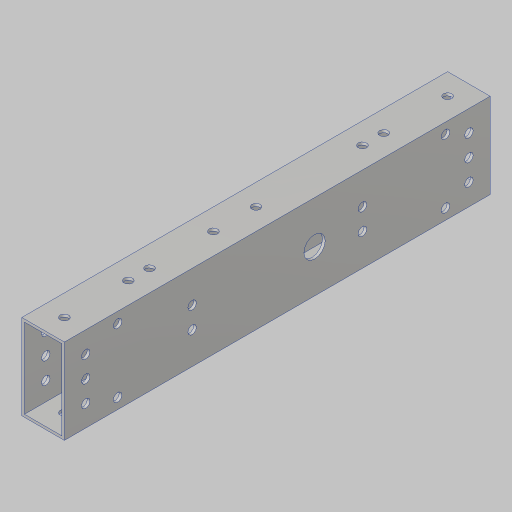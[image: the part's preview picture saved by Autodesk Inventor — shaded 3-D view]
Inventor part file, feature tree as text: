
AUTODESK INVENTOR PART (.ipt)
format: ipt  version: 2023.5 (Build 275446000, 446)  size: 222,720 bytes
history: native  units: in
note: dims shown in document units (in); Inventor stores cm internally (conversion verified against a paired STEP export)
features: sketch x8, hole x7, projected_geometry x3, extrude x2, mirror x1
ambient origin geometry x8: Origin, YZ Plane, XZ Plane, XY Plane, X Axis, Y Axis, Z Axis, Center Point
bodies: Solid1 (feature_tree)
feature tree (21):
  extrude  "Extrusion1"  Depth=0.5in
  hole  "Block Mount Holes"  [1 undecoded]
  hole  "Hole3"  [1 undecoded]
  hole  "Hole5"  [1 undecoded]
  hole  "Hole6"  [1 undecoded]
  sketch  "Sketch10"  dims[d29=0.201in d30=0.75in d31=0.385in d32=0.25in d33=0.5635in d34=1.0in d35=0.8108in d61=0.5in]
  hole  "Hole8"  [1 undecoded]
  hole  "Hole9"  [1 undecoded]
  mirror  "Mirror1"
  extrude  "Extrusion5"  Depth=0.0625in
  hole  "Hole10"  [1 undecoded]
  sketch  "Sketch2"  dims[d4=0.0in d5=0.5in]
  sketch  "Sketch4"  dims[d6=0.5in d7=0.5in]
  sketch  "Sketch8"  dims[d8=0.5in]
  sketch  "Sketch9"  dims[d9=0.201in d10=0.75in d11=0.385in d12=0.25in d13=0.5635in d14=1.0in d15=0.8108in]
  sketch  "Sketch11"  dims[d65=5.0in d66=0.5in]
  sketch  "Sketch13"  dims[d67=1.0in d68=1.0in]
  sketch  "Sketch14"  dims[d69=0.201in d70=0.75in d71=0.385in d72=0.25in d73=0.5635in d74=1.0in d75=0.8108in d79=0.5in d80=0.5in d81=0.201in d82=0.75in d83=0.385in d84=0.25in d85=0.5635in d86=1.0in d87=0.8108in d88=2.75in d89=1.175in d97=4.125in d98=0.201in d99=0.75in d100=0.375in d101=0.25in d102=0.5635in d103=1.0in d104=0.8108in d105=3.0in d106=0.5in d107=0.201in d108=0.75in d109=0.375in d110=0.25in d111=0.5635in d112=1.0in d113=0.8108in d117=0.5in d118=1.0in d119=0.0in d120=1.5in d121=1.0497in d122=0.201in d123=0.38in d124=0.385in d125=0.25in d126=0.5635in d127=1.0in d128=0.8108in d129=1.5in d130=1.25in d44=1.0in d45=1.0in d46=1.0in d47=0.15in d48=0.25in d49=0.375in d50=0.5635in d51=0.75in d52=0.8108in d53=0.0625in d54=0.75in d55=0.375in]
  projected_geometry  "Project Cut Edges1"
  projected_geometry  "Project Cut Edges4"
  projected_geometry  "Project Cut Edges6"
note: 7 required parameter values undecoded (feature->parameter linkage not recoverable at this tier; creation-order binding heuristic only, values carry confidence <= 0.55)
